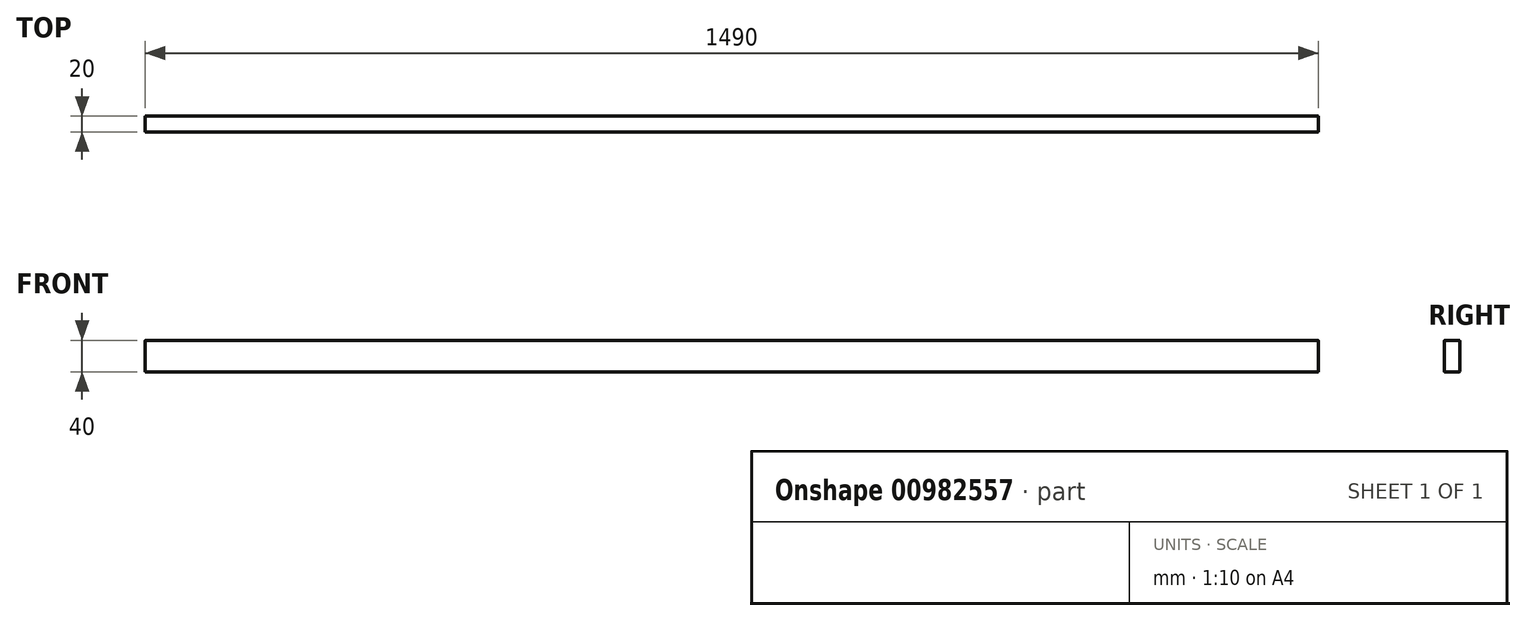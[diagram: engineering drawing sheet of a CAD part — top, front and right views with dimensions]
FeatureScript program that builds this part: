
annotation { "Feature Type Name" : "Feature", "Feature Type Description" : "" }
export const myFeature = defineFeature(function(context is Context, id is Id, definition is map)
    precondition{}
    {
        {
            var Q0;
            Q0=qCreatedBy(makeId("Right.planeOp"),FACE);
            var sketch = newSketch(context, id + "F0", { "sketchPlane" : qUnion([Q0])});
            skLineSegment(sketch, "E0.bottom", {"start": v(-9, 20) * mm, "end": v(9, 20) * mm});
            skLineSegment(sketch, "E0.top", {"start": v(-9, -20) * mm, "end": v(9, -20) * mm});
            skLineSegment(sketch, "E0.left", {"start": v(-10, 19) * mm, "end": v(-10, -19) * mm});
            skLineSegment(sketch, "E0.right", {"start": v(10, 19) * mm, "end": v(10, -19) * mm});
            skPoint(sketch, "E1.visualSharp", {"position": v(-10, 20) * mm});
            skArc(sketch, "E1.filletArc", {"start": v(-9, 20) * mm, "mid": v(-9.7, 19.7) * mm, "end": v(-10, 19) * mm});
            skPoint(sketch, "E2.visualSharp", {"position": v(10, 20) * mm});
            skArc(sketch, "E2.filletArc", {"start": v(10, 19) * mm, "mid": v(9.7, 19.7) * mm, "end": v(9, 20) * mm});
            skPoint(sketch, "E3.visualSharp", {"position": v(10, -20) * mm});
            skArc(sketch, "E3.filletArc", {"start": v(9, -20) * mm, "mid": v(9.7, -19.7) * mm, "end": v(10, -19) * mm});
            skPoint(sketch, "E4.visualSharp", {"position": v(-10, -20) * mm});
            skArc(sketch, "E4.filletArc", {"start": v(-10, -19) * mm, "mid": v(-9.7, -19.7) * mm, "end": v(-9, -20) * mm});
            skLineSegment(sketch, "E5.0", {"start": v(9.5, 19.5) * mm, "end": v(9.5, -19.5) * mm});
            skLineSegment(sketch, "E5.1", {"start": v(-9.5, 19.5) * mm, "end": v(9.5, 19.5) * mm});
            skLineSegment(sketch, "E5.2", {"start": v(-9.5, 19.5) * mm, "end": v(-9.5, -19.5) * mm});
            skLineSegment(sketch, "E5.3", {"start": v(-9.5, -19.5) * mm, "end": v(9.5, -19.5) * mm});
            skSolve(sketch);
        }
        {
            var Q0;
            Q0 = qSketchRegion(id + "F0", true);
            var Q1;
            Q1=makeQuery(id+"F0.imprint","IMPRINT",FACE,{"disambiguationData":[TD([[makeQuery(id+"F0.imprint","IMPRINT",EDGE,{"derivedFrom":sQuery(id+"F0.wireOp",EDGE,"E5.0")}),-1.0]])]});
            extrude(context, id + "F1", {"entities" : qUnion([Q0, Q1]), "endBound" : BoundingType.SYMMETRIC, "depth" : 1490 * mm, "offsetDistance" : 25 * mm});
        }
    });
